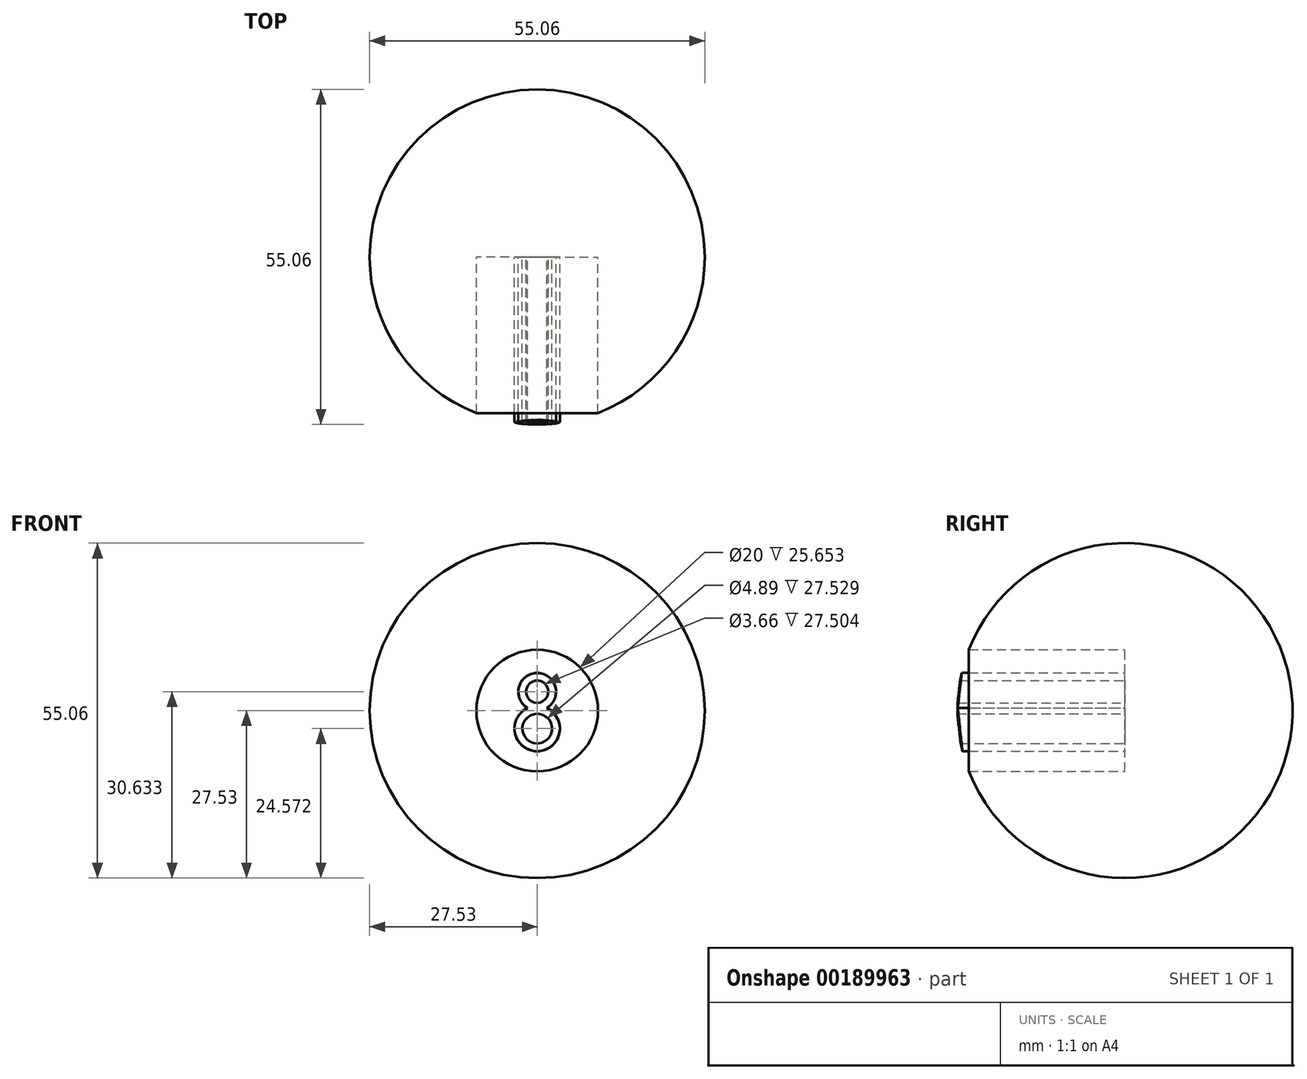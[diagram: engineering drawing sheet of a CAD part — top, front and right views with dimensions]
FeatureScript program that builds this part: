
annotation { "Feature Type Name" : "Feature", "Feature Type Description" : "" }
export const myFeature = defineFeature(function(context is Context, id is Id, definition is map)
    precondition{}
    {
        {
            var Q0;
            Q0=qCreatedBy(makeId("Front.planeOp"),FACE);
            var sketch = newSketch(context, id + "F0", { "sketchPlane" : qUnion([Q0])});
            skCircle(sketch, "E0", {"center": v(0, 0) * mm, "radius": 27.53 * mm});
            skLineSegment(sketch, "E1", {"start": v(-38.58, 0) * mm, "end": v(51.33, 0) * mm});
            skSolve(sketch);
        }
        {
            var Q0;
            {var subQ0=sQuery(id+"F0.wireOp",EDGE,"E1");var subQ1=sQuery(id+"F0.wireOp",EDGE,"E0");var subQ2=makeQuery(id+"F0.imprint","INTERSECT",VERTEX,{"disambiguationData":[OD(0.0)],"derivedFrom":[subQ1,subQ0]});Q0=makeQuery(id+"F0.imprint","IMPRINT",FACE,{"disambiguationData":[TD([[makeQuery(id+"F0.imprint","IMPRINT",EDGE,{"disambiguationData":[TD([[subQ2,-1.0]])],"derivedFrom":subQ1}),1.0]])]});}
            var Q1;
            Q1=sQuery(id+"F0.wireOp",EDGE,"E1");
            revolve(context, id + "F1", {"entities" : qUnion([Q0]), "axis" : qUnion([Q1]), "revolveType" : RevolveType.FULL});
        }
        {
            var Q0;
            Q0=qCreatedBy(makeId("Front.planeOp"),FACE);
            var sketch = newSketch(context, id + "F2", { "sketchPlane" : qUnion([Q0])});
            skCircle(sketch, "E2", {"center": v(0, 0) * mm, "radius": 10 * mm});
            skArc(sketch, "E3", {"start": v(1.58, 0.43) * mm, "mid": v(0, 6.2) * mm, "end": v(-1.58, 0.43) * mm});
            skArc(sketch, "E4", {"start": v(-1.58, 0.43) * mm, "mid": v(0, -6.68) * mm, "end": v(1.58, 0.43) * mm});
            skSolve(sketch);
        }
        {
            var Q0;
            Q0 = qSketchRegion(id + "F2", true);
            extrude(context, id + "F3", {"entities" : qUnion([Q0]), "operationType" : NewBodyOperationType.REMOVE, "endBound" : BoundingType.UP_TO_NEXT, "depth" : 25 * mm});
        }
        {
            var Q0;
            Q0=qCreatedBy(makeId("Front.planeOp"),FACE);
            var sketch = newSketch(context, id + "F4", { "sketchPlane" : qUnion([Q0])});
            skCircle(sketch, "E5", {"center": v(0, 3.1) * mm, "radius": 1.83 * mm});
            skCircle(sketch, "E6", {"center": v(0, -2.96) * mm, "radius": 2.44 * mm});
            skSolve(sketch);
        }
        {
            var Q0;
            Q0 = qSketchRegion(id + "F4", true);
            extrude(context, id + "F5", {"entities" : qUnion([Q0]), "operationType" : NewBodyOperationType.REMOVE, "endBound" : BoundingType.UP_TO_NEXT, "depth" : 25 * mm});
        }
    });
